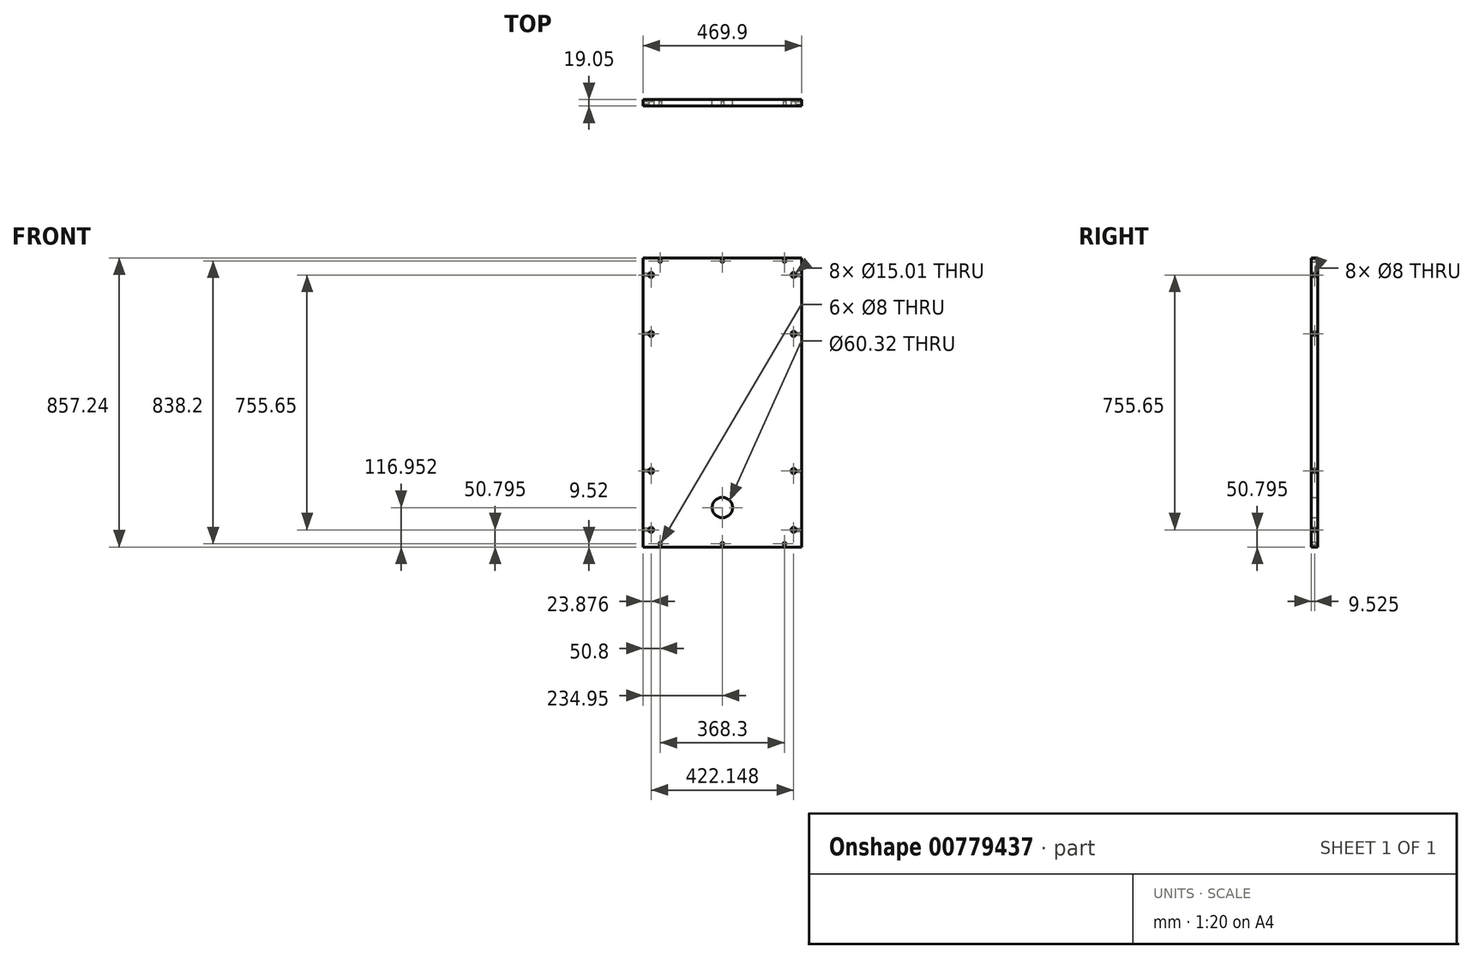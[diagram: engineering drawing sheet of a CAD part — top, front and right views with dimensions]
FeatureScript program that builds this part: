
annotation { "Feature Type Name" : "Feature", "Feature Type Description" : "" }
export const myFeature = defineFeature(function(context is Context, id is Id, definition is map)
    precondition{}
    {
        {
            var Q0;
            Q0=qCreatedBy(makeId("Front.planeOp"),FACE);
            var sketch = newSketch(context, id + "F0", { "sketchPlane" : qUnion([Q0])});
            skLineSegment(sketch, "E0.bottom", {"start": v(234.95, 428.63) * mm, "end": v(-234.95, 428.63) * mm});
            skLineSegment(sketch, "E0.top", {"start": v(234.95, -428.63) * mm, "end": v(-234.95, -428.63) * mm});
            skLineSegment(sketch, "E0.left", {"start": v(234.95, 428.62) * mm, "end": v(234.95, -428.63) * mm});
            skLineSegment(sketch, "E0.right", {"start": v(-234.95, 428.63) * mm, "end": v(-234.95, -428.63) * mm});
            skPoint(sketch, "E0.middle", {"position": v(0, 0) * mm});
            skLineSegment(sketch, "E1", {"start": v(0, -413.27) * mm, "end": v(0, -311.67) * mm});
            skPoint(sketch, "E1.startSnap0", {"position": v(0, -428.63) * mm});
            skCircle(sketch, "E2", {"center": v(0, -311.67) * mm, "radius": 30.16 * mm});
            skSolve(sketch);
        }
        {
            var Q0;
            Q0=makeQuery(id+"F0.imprint","IMPRINT",FACE,{"disambiguationData":[TD([[makeQuery(id+"F0.imprint","IMPRINT",EDGE,{"derivedFrom":sQuery(id+"F0.wireOp",EDGE,"E0.bottom")}),1.0]])]});
            extrude(context, id + "F1", {"entities" : qUnion([Q0]), "depth" : 19.05 * mm, "offsetDistance" : 25.4 * mm});
        }
        {
            var Q0;
            Q0=makeQuery(id+"F1.opExtrude","CAP_FACE",FACE,{"disambiguationData":[OSD([sQuery(id+"F0.wireOp",EDGE,"E0.bottom"),sQuery(id+"F0.wireOp",EDGE,"E0.top"),sQuery(id+"F0.wireOp",EDGE,"E0.left"),sQuery(id+"F0.wireOp",EDGE,"E0.right"),sQuery(id+"F0.wireOp",EDGE,"E2")])],"isStart":false});
            var sketch = newSketch(context, id + "F2", { "sketchPlane" : qUnion([Q0])});
            skLineSegment(sketch, "E3", {"start": v(-234.95, 428.63) * mm, "end": v(-234.95, 419.1) * mm});
            skLineSegment(sketch, "E4", {"start": v(-234.95, 419.1) * mm, "end": v(-184.15, 419.1) * mm});
            skLineSegment(sketch, "E5", {"start": v(234.95, 428.63) * mm, "end": v(234.95, 419.1) * mm});
            skLineSegment(sketch, "E6", {"start": v(234.95, 419.1) * mm, "end": v(184.15, 419.1) * mm});
            skPoint(sketch, "E7", {"position": v(-184.15, 419.1) * mm});
            skPoint(sketch, "E8", {"position": v(184.15, 419.1) * mm});
            skLineSegment(sketch, "E9", {"start": v(0, 428.63) * mm, "end": v(0, 419.1) * mm});
            skPoint(sketch, "E10", {"position": v(0, 419.1) * mm});
            skLineSegment(sketch, "E11", {"start": v(-234.95, -428.63) * mm, "end": v(-234.95, -419.1) * mm});
            skLineSegment(sketch, "E12", {"start": v(-234.95, -419.1) * mm, "end": v(-184.15, -419.1) * mm});
            skLineSegment(sketch, "E13", {"start": v(234.95, -428.63) * mm, "end": v(234.95, -419.1) * mm});
            skLineSegment(sketch, "E14", {"start": v(234.95, -419.1) * mm, "end": v(184.15, -419.1) * mm});
            skLineSegment(sketch, "E15", {"start": v(0, -428.63) * mm, "end": v(0, -419.1) * mm});
            skPoint(sketch, "E16", {"position": v(-184.15, -419.1) * mm});
            skPoint(sketch, "E17", {"position": v(0, -419.1) * mm});
            skPoint(sketch, "E18", {"position": v(184.15, -419.1) * mm});
            skSolve(sketch);
        }
        {
            var Q0;
            Q0=sQuery(id+"F2.wireOp",VERTEX,"E7");
            var Q1;
            Q1=sQuery(id+"F2.wireOp",VERTEX,"E10");
            var Q2;
            Q2=sQuery(id+"F2.wireOp",VERTEX,"E8");
            var Q3;
            Q3=sQuery(id+"F2.wireOp",VERTEX,"E16");
            var Q4;
            Q4=sQuery(id+"F2.wireOp",VERTEX,"E17");
            var Q5;
            Q5=sQuery(id+"F2.wireOp",VERTEX,"E18");
            var Q6;
            Q6=makeQuery(id+"F1.opExtrude","SWEPT_BODY",BODY,{"disambiguationData":[OSD([sQuery(id+"F0.wireOp",EDGE,"E0.bottom"),sQuery(id+"F0.wireOp",EDGE,"E0.top"),sQuery(id+"F0.wireOp",EDGE,"E0.left"),sQuery(id+"F0.wireOp",EDGE,"E0.right"),sQuery(id+"F0.wireOp",EDGE,"E2")])]});
            hole(context, id + "F3", {"style" : HoleStyle.SIMPLE, "endStyle" : HoleEndStyle.BLIND, "holeDiameter" : 8 * mm, "majorDiameter" : 6.35 * mm, "holeDepth" : 14.22 * mm, "isTappedThrough" : true, "tappedDepth" : 12.7 * mm, "tapClearance" : 3, "startFromSketch" : true, "locations" : qUnion([Q0, Q1, Q2, Q3, Q4, Q5]), "scope" : qUnion([Q6])});
        }
        {
            var Q0;
            Q0=makeQuery(id+"F1.opExtrude","CAP_FACE",FACE,{"disambiguationData":[OSD([sQuery(id+"F0.wireOp",EDGE,"E0.bottom"),sQuery(id+"F0.wireOp",EDGE,"E0.top"),sQuery(id+"F0.wireOp",EDGE,"E0.left"),sQuery(id+"F0.wireOp",EDGE,"E0.right"),sQuery(id+"F0.wireOp",EDGE,"E2")])],"isStart":false});
            var sketch = newSketch(context, id + "F4", { "sketchPlane" : qUnion([Q0])});
            skLineSegment(sketch, "E19", {"start": v(-234.95, 428.63) * mm, "end": v(-211.07, 428.63) * mm});
            skLineSegment(sketch, "E20", {"start": v(-211.07, 428.63) * mm, "end": v(-211.07, 377.83) * mm});
            skLineSegment(sketch, "E21", {"start": v(-234.95, -428.63) * mm, "end": v(-211.07, -428.63) * mm});
            skLineSegment(sketch, "E22", {"start": v(-211.07, -428.63) * mm, "end": v(-211.07, -377.83) * mm});
            skLineSegment(sketch, "E23", {"start": v(234.95, 428.63) * mm, "end": v(211.07, 428.63) * mm});
            skLineSegment(sketch, "E24", {"start": v(211.07, 428.63) * mm, "end": v(211.07, 377.83) * mm});
            skLineSegment(sketch, "E25", {"start": v(234.95, -428.63) * mm, "end": v(211.07, -428.63) * mm});
            skLineSegment(sketch, "E26", {"start": v(211.07, -428.63) * mm, "end": v(211.07, -377.83) * mm});
            skLineSegment(sketch, "E27", {"start": v(-234.95, 0) * mm, "end": v(-211.07, 0) * mm});
            skLineSegment(sketch, "E28", {"start": v(-211.07, 0) * mm, "end": v(-211.07, 203.2) * mm});
            skLineSegment(sketch, "E29", {"start": v(-211.07, 0) * mm, "end": v(-211.07, -203.2) * mm});
            skLineSegment(sketch, "E30", {"start": v(234.95, 0) * mm, "end": v(211.07, 0) * mm});
            skLineSegment(sketch, "E31", {"start": v(211.07, 0) * mm, "end": v(211.07, 203.2) * mm});
            skLineSegment(sketch, "E32", {"start": v(211.07, 0) * mm, "end": v(211.07, -203.2) * mm});
            skPoint(sketch, "E33", {"position": v(-211.07, 377.83) * mm});
            skPoint(sketch, "E34", {"position": v(211.07, 377.83) * mm});
            skPoint(sketch, "E35", {"position": v(211.07, 203.2) * mm});
            skPoint(sketch, "E36", {"position": v(-211.07, 203.2) * mm});
            skPoint(sketch, "E37", {"position": v(-211.07, -203.2) * mm});
            skPoint(sketch, "E38", {"position": v(211.07, -203.2) * mm});
            skPoint(sketch, "E39", {"position": v(211.07, -377.83) * mm});
            skPoint(sketch, "E40", {"position": v(-211.07, -377.83) * mm});
            skSolve(sketch);
        }
        {
            var Q0;
            Q0=sQuery(id+"F4.wireOp",VERTEX,"E33");
            var Q1;
            Q1=sQuery(id+"F4.wireOp",VERTEX,"E34");
            var Q2;
            Q2=sQuery(id+"F4.wireOp",VERTEX,"E35");
            var Q3;
            Q3=sQuery(id+"F4.wireOp",VERTEX,"E36");
            var Q4;
            Q4=sQuery(id+"F4.wireOp",VERTEX,"E37");
            var Q5;
            Q5=sQuery(id+"F4.wireOp",VERTEX,"E38");
            var Q6;
            Q6=sQuery(id+"F4.wireOp",VERTEX,"E39");
            var Q7;
            Q7=sQuery(id+"F4.wireOp",VERTEX,"E40");
            var Q8;
            Q8=makeQuery(id+"F1.opExtrude","SWEPT_BODY",BODY,{"disambiguationData":[OSD([sQuery(id+"F0.wireOp",EDGE,"E0.bottom"),sQuery(id+"F0.wireOp",EDGE,"E0.top"),sQuery(id+"F0.wireOp",EDGE,"E0.left"),sQuery(id+"F0.wireOp",EDGE,"E0.right"),sQuery(id+"F0.wireOp",EDGE,"E2")])]});
            hole(context, id + "F5", {"style" : HoleStyle.SIMPLE, "endStyle" : HoleEndStyle.BLIND, "holeDiameter" : 15 * mm, "majorDiameter" : 6.35 * mm, "holeDepth" : 14.22 * mm, "isTappedThrough" : true, "tappedDepth" : 12.7 * mm, "tapClearance" : 3, "startFromSketch" : true, "locations" : qUnion([Q0, Q1, Q2, Q3, Q4, Q5, Q6, Q7]), "scope" : qUnion([Q8])});
        }
        {
            var Q0;
            Q0=makeQuery(id+"F1.opExtrude","SWEPT_FACE",FACE,{"disambiguationData":[OSD([sQuery(id+"F0.wireOp",EDGE,"E0.left")])]});
            var sketch = newSketch(context, id + "F6", { "sketchPlane" : qUnion([Q0])});
            skLineSegment(sketch, "E41", {"start": v(-9.53, 428.63) * mm, "end": v(-9.53, 377.83) * mm});
            skLineSegment(sketch, "E42", {"start": v(-9.53, -428.63) * mm, "end": v(-9.53, -377.83) * mm});
            skLineSegment(sketch, "E43", {"start": v(-9.53, 0) * mm, "end": v(-9.53, -203.2) * mm});
            skPoint(sketch, "E43.startSnap0", {"position": v(0, 0) * mm});
            skLineSegment(sketch, "E44", {"start": v(-9.53, 0) * mm, "end": v(-9.53, 203.2) * mm});
            skPoint(sketch, "E45", {"position": v(-9.53, 377.83) * mm});
            skPoint(sketch, "E46", {"position": v(-9.53, 203.2) * mm});
            skPoint(sketch, "E47", {"position": v(-9.53, -203.2) * mm});
            skPoint(sketch, "E48", {"position": v(-9.53, -377.83) * mm});
            skSolve(sketch);
        }
        {
            var Q0;
            Q0=sQuery(id+"F6.wireOp",VERTEX,"E45");
            var Q1;
            Q1=sQuery(id+"F6.wireOp",VERTEX,"E46");
            var Q2;
            Q2=sQuery(id+"F6.wireOp",VERTEX,"E47");
            var Q3;
            Q3=sQuery(id+"F6.wireOp",VERTEX,"E48");
            var Q4;
            Q4=makeQuery(id+"F1.opExtrude","SWEPT_BODY",BODY,{"disambiguationData":[OSD([sQuery(id+"F0.wireOp",EDGE,"E0.bottom"),sQuery(id+"F0.wireOp",EDGE,"E0.top"),sQuery(id+"F0.wireOp",EDGE,"E0.left"),sQuery(id+"F0.wireOp",EDGE,"E0.right"),sQuery(id+"F0.wireOp",EDGE,"E2")])]});
            hole(context, id + "F7", {"style" : HoleStyle.SIMPLE, "endStyle" : HoleEndStyle.BLIND, "holeDiameter" : 8 * mm, "majorDiameter" : 6.35 * mm, "holeDepth" : 25.4 * mm, "isTappedThrough" : true, "tappedDepth" : 12.7 * mm, "tapClearance" : 3, "startFromSketch" : true, "locations" : qUnion([Q0, Q1, Q2, Q3]), "scope" : qUnion([Q4])});
        }
        {
            var Q0;
            Q0=makeQuery(id+"F1.opExtrude","SWEPT_FACE",FACE,{"disambiguationData":[OSD([sQuery(id+"F0.wireOp",EDGE,"E0.right")])]});
            var sketch = newSketch(context, id + "F8", { "sketchPlane" : qUnion([Q0])});
            skLineSegment(sketch, "E49", {"start": v(9.53, 428.63) * mm, "end": v(9.53, 377.83) * mm});
            skLineSegment(sketch, "E50", {"start": v(9.53, -428.63) * mm, "end": v(9.53, -377.83) * mm});
            skLineSegment(sketch, "E51", {"start": v(19.05, 0) * mm, "end": v(9.53, 0) * mm});
            skLineSegment(sketch, "E52", {"start": v(9.53, 0) * mm, "end": v(9.53, 203.2) * mm});
            skLineSegment(sketch, "E53", {"start": v(9.53, 0) * mm, "end": v(9.53, -203.2) * mm});
            skPoint(sketch, "E54", {"position": v(9.53, 377.83) * mm});
            skPoint(sketch, "E55", {"position": v(9.53, 203.2) * mm});
            skPoint(sketch, "E56", {"position": v(9.53, -203.2) * mm});
            skPoint(sketch, "E57", {"position": v(9.53, -377.83) * mm});
            skSolve(sketch);
        }
        {
            var Q0;
            Q0=sQuery(id+"F8.wireOp",VERTEX,"E54");
            var Q1;
            Q1=sQuery(id+"F8.wireOp",VERTEX,"E55");
            var Q2;
            Q2=sQuery(id+"F8.wireOp",VERTEX,"E56");
            var Q3;
            Q3=sQuery(id+"F8.wireOp",VERTEX,"E57");
            var Q4;
            Q4=makeQuery(id+"F1.opExtrude","SWEPT_BODY",BODY,{"disambiguationData":[OSD([sQuery(id+"F0.wireOp",EDGE,"E0.bottom"),sQuery(id+"F0.wireOp",EDGE,"E0.top"),sQuery(id+"F0.wireOp",EDGE,"E0.left"),sQuery(id+"F0.wireOp",EDGE,"E0.right"),sQuery(id+"F0.wireOp",EDGE,"E2")])]});
            hole(context, id + "F9", {"style" : HoleStyle.SIMPLE, "endStyle" : HoleEndStyle.BLIND, "holeDiameter" : 8 * mm, "majorDiameter" : 6.35 * mm, "holeDepth" : 25.4 * mm, "isTappedThrough" : true, "tappedDepth" : 12.7 * mm, "tapClearance" : 3, "startFromSketch" : true, "locations" : qUnion([Q0, Q1, Q2, Q3]), "scope" : qUnion([Q4])});
        }
    });
